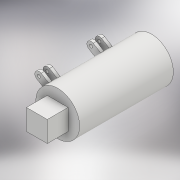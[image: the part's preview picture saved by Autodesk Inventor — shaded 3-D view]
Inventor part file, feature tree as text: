
AUTODESK INVENTOR PART (.ipt)
format: ipt  version: 2018 (Build 220112000, 112)  size: 173,056 bytes
history: native  units: mm
features: extrude x3, sketch x2, pattern_linear x2, plane x1
ambient origin geometry x8: Origin, YZ Plane, XZ Plane, XY Plane, X Axis, Y Axis, Z Axis, Center Point
bodies: Solid1 (feature_tree)
feature tree (8):
  sketch  "Sketch1"  dims[d0=42.0mm d1=20.0mm]
  extrude  "Extrusion1"  Depth=20.0mm
  extrude  "Extrusion2"  Depth=90.0mm TaperAngle=0.0deg
  plane  "Work Plane1"
  extrude  "Extrusion3"  Depth=20.0mm TaperAngle=0.0deg
  pattern_linear  "Rectangular Pattern2"  Spacing1=-10.0mm  [1 undecoded]
  pattern_linear  "Rectangular Pattern1"  Spacing1=3.0mm  [1 undecoded]
  sketch  "Sketch2"  dims[d2=20.0mm d3=90.0mm d4=0.0mm d5=20.0mm d6=0.0mm d7=-10.0mm d8=3.0mm d9=30.0mm d10=15.0mm d11=4.0mm d12=4.0mm d13=4.0mm d14=3.0mm d15=0.0mm d16=20.0mm d18=50.0mm d19=20.0mm d21=8.0mm]
note: 2 required parameter values undecoded (feature->parameter linkage not recoverable at this tier; creation-order binding heuristic only, values carry confidence <= 0.55)
